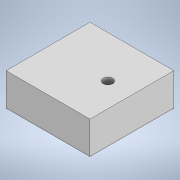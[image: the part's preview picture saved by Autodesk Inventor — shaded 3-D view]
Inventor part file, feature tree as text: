
AUTODESK INVENTOR PART (.ipt)
format: ipt  version: 2020.2 (Build 242310000, 310)  size: 188,416 bytes
history: native  units: mm
features: extrude x5, sketch x5, fillet x3
ambient origin geometry x8: Origin, YZ Plane, XZ Plane, XY Plane, X Axis, Y Axis, Z Axis, Center Point
bodies: Solide1 (feature_tree)
feature tree (13):
  extrude  "Extrusion1"  Depth=20.0mm
  extrude  "Extrusion2"  Depth=70.0mm TaperAngle=0.0deg
  extrude  "Extrusion4"  Depth=35.0mm
  fillet  "Congé3"  Radius=20.0mm
  fillet  "Congé4"  Radius=70.0mm
  extrude  "Extrusion5"  Depth=8.0mm
  fillet  "Congé5"  Radius=18.0mm
  extrude  "Extrusion6"  Depth=66.0mm
  sketch  "Esquisse1"
  sketch  "Esquisse2"
  sketch  "Esquisse4"
  sketch  "Esquisse5"
  sketch  "Esquisse6"
